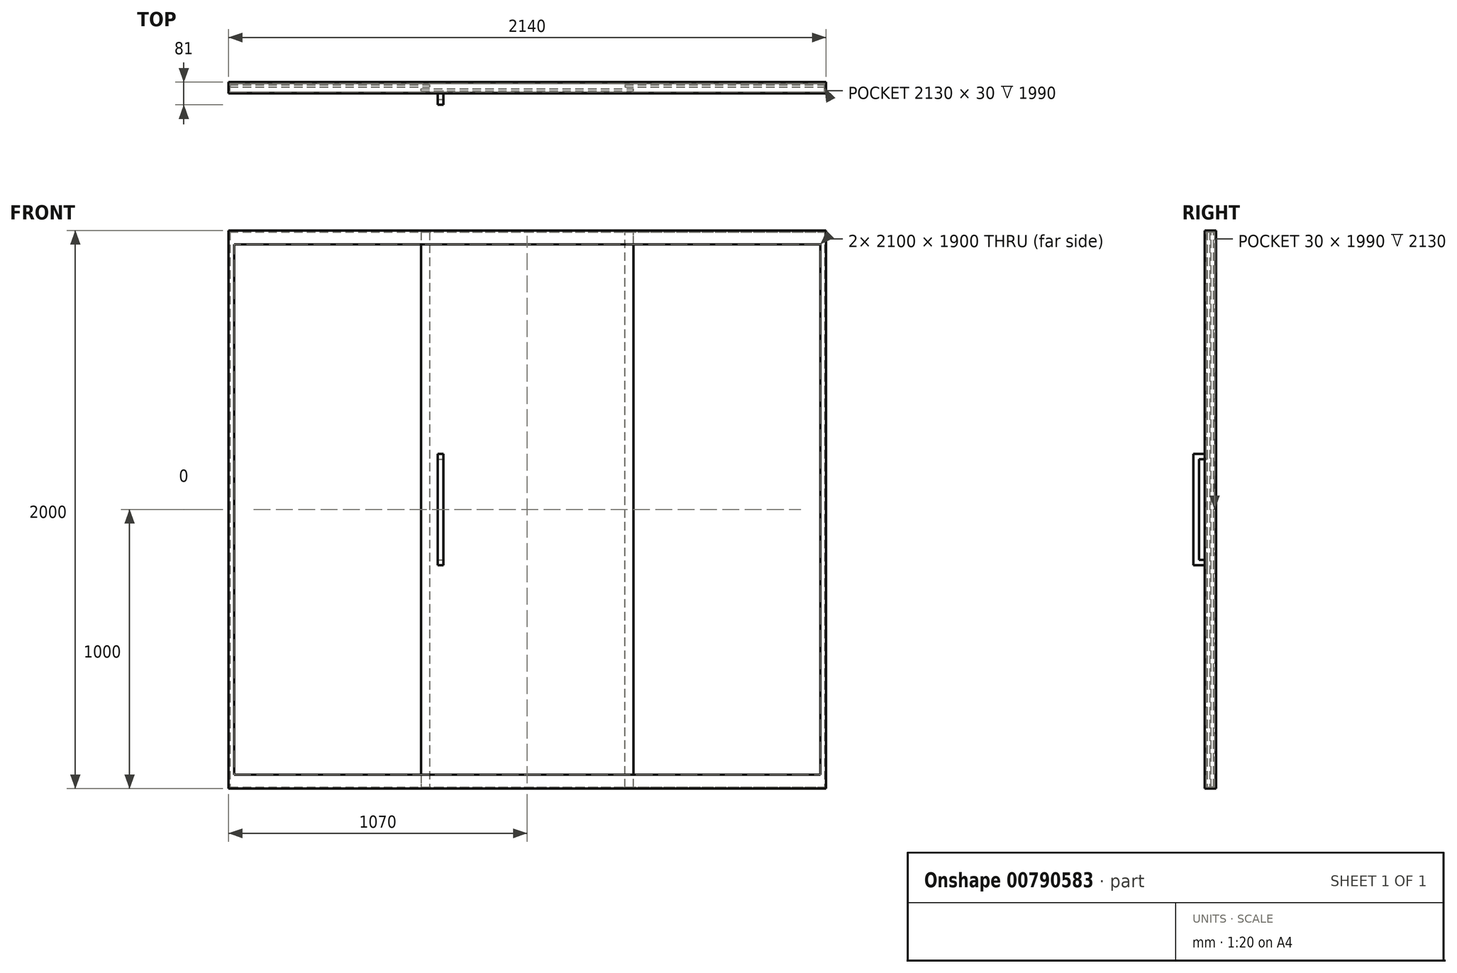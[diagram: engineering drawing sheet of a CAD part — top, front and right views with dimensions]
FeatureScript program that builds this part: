
annotation { "Feature Type Name" : "Feature", "Feature Type Description" : "" }
export const myFeature = defineFeature(function(context is Context, id is Id, definition is map)
    precondition{}
    {
        {
            var Q0;
            Q0=qCreatedBy(makeId("Front.planeOp"),FACE);
            var sketch = newSketch(context, id + "F0", { "sketchPlane" : qUnion([Q0])});
            skLineSegment(sketch, "E0.bottom", {"start": v(0, 0) * mm, "end": v(2140, 0) * mm});
            skLineSegment(sketch, "E0.top", {"start": v(0, 2000) * mm, "end": v(2140, 2000) * mm});
            skLineSegment(sketch, "E0.left", {"start": v(0, 0) * mm, "end": v(0, 2000) * mm});
            skLineSegment(sketch, "E0.right", {"start": v(2140, 0) * mm, "end": v(2140, 2000) * mm});
            skLineSegment(sketch, "E1.bottom", {"start": v(5, 1995) * mm, "end": v(2135, 1995) * mm});
            skLineSegment(sketch, "E1.top", {"start": v(5, 5) * mm, "end": v(2135, 5) * mm});
            skLineSegment(sketch, "E1.left", {"start": v(5, 1995) * mm, "end": v(5, 5) * mm});
            skLineSegment(sketch, "E1.right", {"start": v(2135, 1995) * mm, "end": v(2135, 5) * mm});
            skLineSegment(sketch, "E2.bottom", {"start": v(20, 1950) * mm, "end": v(2120, 1950) * mm});
            skLineSegment(sketch, "E2.top", {"start": v(20, 50) * mm, "end": v(2120, 50) * mm});
            skLineSegment(sketch, "E2.left", {"start": v(20, 1950) * mm, "end": v(20, 50) * mm});
            skLineSegment(sketch, "E2.right", {"start": v(2120, 1950) * mm, "end": v(2120, 50) * mm});
            skLineSegment(sketch, "E3", {"start": v(720, 1995) * mm, "end": v(720, 5) * mm});
            skLineSegment(sketch, "E4", {"start": v(1420, 5) * mm, "end": v(1420, 1995) * mm});
            skLineSegment(sketch, "E5", {"start": v(720, 1000) * mm, "end": v(5, 1000) * mm, "construction": true});
            skLineSegment(sketch, "E6", {"start": v(1420, 1000) * mm, "end": v(2135, 1000) * mm, "construction": true});
            skLineSegment(sketch, "E7", {"start": v(690, 1995) * mm, "end": v(690, 5) * mm});
            skLineSegment(sketch, "E8", {"start": v(1450, 5) * mm, "end": v(1450, 1995) * mm});
            skSolve(sketch);
        }
        {
            var Q0;
            {var subQ4=sQuery(id+"F0.wireOp",EDGE,"E1.left");Q0=makeQuery(id+"F0.imprint","IMPRINT",FACE,{"disambiguationData":[TD([[makeQuery(id+"F0.imprint","IMPRINT",EDGE,{"derivedFrom":subQ4}),1.0]])]});}
            var Q1;
            Q1=makeQuery(id+"F0.imprint","IMPRINT",FACE,{"disambiguationData":[TD([[makeQuery(id+"F0.imprint","IMPRINT",EDGE,{"derivedFrom":sQuery(id+"F0.wireOp",EDGE,"E0.bottom")}),1.0]])]});
            var Q2;
            {var subQ0=sQuery(id+"F0.wireOp",EDGE,"E3");var subQ1=sQuery(id+"F0.wireOp",EDGE,"E1.bottom");var subQ2=makeQuery(id+"F0.imprint","INTERSECT",VERTEX,{"derivedFrom":[subQ1,subQ0]});Q2=makeQuery(id+"F0.imprint","IMPRINT",FACE,{"disambiguationData":[TD([[makeQuery(id+"F0.imprint","IMPRINT",EDGE,{"disambiguationData":[TD([[subQ2,1.0]])],"derivedFrom":subQ1}),-1.0]])]});}
            var Q3;
            {var subQ0=sQuery(id+"F0.wireOp",EDGE,"E3");var subQ1=sQuery(id+"F0.wireOp",EDGE,"E1.bottom");var subQ2=makeQuery(id+"F0.imprint","INTERSECT",VERTEX,{"derivedFrom":[subQ1,subQ0]});Q3=makeQuery(id+"F0.imprint","IMPRINT",FACE,{"disambiguationData":[TD([[makeQuery(id+"F0.imprint","IMPRINT",EDGE,{"disambiguationData":[TD([[subQ2,-1.0]])],"derivedFrom":subQ1}),-1.0]])]});}
            var Q4;
            {var subQ4=sQuery(id+"F0.wireOp",EDGE,"E1.right");Q4=makeQuery(id+"F0.imprint","IMPRINT",FACE,{"disambiguationData":[TD([[makeQuery(id+"F0.imprint","IMPRINT",EDGE,{"derivedFrom":subQ4}),-1.0]])]});}
            var Q5;
            {var subQ0=sQuery(id+"F0.wireOp",EDGE,"E4");var subQ1=sQuery(id+"F0.wireOp",EDGE,"E1.bottom");var subQ2=makeQuery(id+"F0.imprint","INTERSECT",VERTEX,{"derivedFrom":[subQ1,subQ0]});Q5=makeQuery(id+"F0.imprint","IMPRINT",FACE,{"disambiguationData":[TD([[makeQuery(id+"F0.imprint","IMPRINT",EDGE,{"disambiguationData":[TD([[subQ2,-1.0]])],"derivedFrom":subQ1}),-1.0]])]});}
            var Q6;
            {var subQ0=sQuery(id+"F0.wireOp",EDGE,"E3");var subQ1=sQuery(id+"F0.wireOp",EDGE,"E1.top");var subQ2=makeQuery(id+"F0.imprint","INTERSECT",VERTEX,{"derivedFrom":[subQ1,subQ0]});Q6=makeQuery(id+"F0.imprint","IMPRINT",FACE,{"disambiguationData":[TD([[makeQuery(id+"F0.imprint","IMPRINT",EDGE,{"disambiguationData":[TD([[subQ2,1.0]])],"derivedFrom":subQ1}),1.0]])]});}
            var Q7;
            {var subQ0=sQuery(id+"F0.wireOp",EDGE,"E3");var subQ1=sQuery(id+"F0.wireOp",EDGE,"E1.top");var subQ2=makeQuery(id+"F0.imprint","INTERSECT",VERTEX,{"derivedFrom":[subQ1,subQ0]});Q7=makeQuery(id+"F0.imprint","IMPRINT",FACE,{"disambiguationData":[TD([[makeQuery(id+"F0.imprint","IMPRINT",EDGE,{"disambiguationData":[TD([[subQ2,-1.0]])],"derivedFrom":subQ1}),1.0]])]});}
            var Q8;
            {var subQ0=sQuery(id+"F0.wireOp",EDGE,"E4");var subQ1=sQuery(id+"F0.wireOp",EDGE,"E1.top");var subQ2=makeQuery(id+"F0.imprint","INTERSECT",VERTEX,{"derivedFrom":[subQ1,subQ0]});Q8=makeQuery(id+"F0.imprint","IMPRINT",FACE,{"disambiguationData":[TD([[makeQuery(id+"F0.imprint","IMPRINT",EDGE,{"disambiguationData":[TD([[subQ2,-1.0]])],"derivedFrom":subQ1}),1.0]])]});}
            extrude(context, id + "F1", {"entities" : qUnion([Q0, Q1, Q2, Q3, Q4, Q5, Q6, Q7, Q8]), "depth" : 20 * mm, "offsetDistance" : 25 * mm, "hasSecondDirection" : true, "secondDirectionOppositeDirection" : true, "secondDirectionDepth" : 20 * mm});
        }
        {
            var Q0;
            {var subQ4=sQuery(id+"F0.wireOp",EDGE,"E1.left");Q0=makeQuery(id+"F0.imprint","IMPRINT",FACE,{"disambiguationData":[TD([[makeQuery(id+"F0.imprint","IMPRINT",EDGE,{"derivedFrom":subQ4}),1.0]])]});}
            var Q1;
            {var subQ0=sQuery(id+"F0.wireOp",EDGE,"E3");var subQ1=sQuery(id+"F0.wireOp",EDGE,"E1.bottom");var subQ2=makeQuery(id+"F0.imprint","INTERSECT",VERTEX,{"derivedFrom":[subQ1,subQ0]});Q1=makeQuery(id+"F0.imprint","IMPRINT",FACE,{"disambiguationData":[TD([[makeQuery(id+"F0.imprint","IMPRINT",EDGE,{"disambiguationData":[TD([[subQ2,1.0]])],"derivedFrom":subQ1}),-1.0]])]});}
            var Q2;
            {var subQ0=sQuery(id+"F0.wireOp",EDGE,"E3");var subQ1=sQuery(id+"F0.wireOp",EDGE,"E1.bottom");var subQ2=makeQuery(id+"F0.imprint","INTERSECT",VERTEX,{"derivedFrom":[subQ1,subQ0]});Q2=makeQuery(id+"F0.imprint","IMPRINT",FACE,{"disambiguationData":[TD([[makeQuery(id+"F0.imprint","IMPRINT",EDGE,{"disambiguationData":[TD([[subQ2,-1.0]])],"derivedFrom":subQ1}),-1.0]])]});}
            var Q3;
            {var subQ0=sQuery(id+"F0.wireOp",EDGE,"E4");var subQ1=sQuery(id+"F0.wireOp",EDGE,"E1.bottom");var subQ2=makeQuery(id+"F0.imprint","INTERSECT",VERTEX,{"derivedFrom":[subQ1,subQ0]});Q3=makeQuery(id+"F0.imprint","IMPRINT",FACE,{"disambiguationData":[TD([[makeQuery(id+"F0.imprint","IMPRINT",EDGE,{"disambiguationData":[TD([[subQ2,-1.0]])],"derivedFrom":subQ1}),-1.0]])]});}
            var Q4;
            {var subQ4=sQuery(id+"F0.wireOp",EDGE,"E1.right");Q4=makeQuery(id+"F0.imprint","IMPRINT",FACE,{"disambiguationData":[TD([[makeQuery(id+"F0.imprint","IMPRINT",EDGE,{"derivedFrom":subQ4}),-1.0]])]});}
            var Q5;
            {var subQ0=sQuery(id+"F0.wireOp",EDGE,"E3");var subQ1=sQuery(id+"F0.wireOp",EDGE,"E1.top");var subQ2=makeQuery(id+"F0.imprint","INTERSECT",VERTEX,{"derivedFrom":[subQ1,subQ0]});Q5=makeQuery(id+"F0.imprint","IMPRINT",FACE,{"disambiguationData":[TD([[makeQuery(id+"F0.imprint","IMPRINT",EDGE,{"disambiguationData":[TD([[subQ2,1.0]])],"derivedFrom":subQ1}),1.0]])]});}
            var Q6;
            {var subQ0=sQuery(id+"F0.wireOp",EDGE,"E3");var subQ1=sQuery(id+"F0.wireOp",EDGE,"E1.top");var subQ2=makeQuery(id+"F0.imprint","INTERSECT",VERTEX,{"derivedFrom":[subQ1,subQ0]});Q6=makeQuery(id+"F0.imprint","IMPRINT",FACE,{"disambiguationData":[TD([[makeQuery(id+"F0.imprint","IMPRINT",EDGE,{"disambiguationData":[TD([[subQ2,-1.0]])],"derivedFrom":subQ1}),1.0]])]});}
            var Q7;
            {var subQ0=sQuery(id+"F0.wireOp",EDGE,"E4");var subQ1=sQuery(id+"F0.wireOp",EDGE,"E1.top");var subQ2=makeQuery(id+"F0.imprint","INTERSECT",VERTEX,{"derivedFrom":[subQ1,subQ0]});Q7=makeQuery(id+"F0.imprint","IMPRINT",FACE,{"disambiguationData":[TD([[makeQuery(id+"F0.imprint","IMPRINT",EDGE,{"disambiguationData":[TD([[subQ2,-1.0]])],"derivedFrom":subQ1}),1.0]])]});}
            extrude(context, id + "F2", {"entities" : qUnion([Q0, Q1, Q2, Q3, Q4, Q5, Q6, Q7]), "operationType" : NewBodyOperationType.REMOVE, "depth" : 15 * mm, "offsetDistance" : 25 * mm, "hasSecondDirection" : true, "secondDirectionOppositeDirection" : true, "secondDirectionDepth" : 15 * mm});
        }
        {
            var Q0;
            {var subQ0=sQuery(id+"F0.wireOp",EDGE,"E2.left");Q0=makeQuery(id+"F0.imprint","IMPRINT",FACE,{"disambiguationData":[TD([[makeQuery(id+"F0.imprint","IMPRINT",EDGE,{"derivedFrom":subQ0}),1.0]])]});}
            var Q1;
            {var subQ0=sQuery(id+"F0.wireOp",EDGE,"E2.right");Q1=makeQuery(id+"F0.imprint","IMPRINT",FACE,{"disambiguationData":[TD([[makeQuery(id+"F0.imprint","IMPRINT",EDGE,{"derivedFrom":subQ0}),-1.0]])]});}
            var Q2;
            {var subQ4=sQuery(id+"F0.wireOp",EDGE,"E1.right");Q2=makeQuery(id+"F0.imprint","IMPRINT",FACE,{"disambiguationData":[TD([[makeQuery(id+"F0.imprint","IMPRINT",EDGE,{"derivedFrom":subQ4}),-1.0]])]});}
            var Q3;
            {var subQ4=sQuery(id+"F0.wireOp",EDGE,"E1.left");Q3=makeQuery(id+"F0.imprint","IMPRINT",FACE,{"disambiguationData":[TD([[makeQuery(id+"F0.imprint","IMPRINT",EDGE,{"derivedFrom":subQ4}),1.0]])]});}
            var Q4;
            {var subQ0=sQuery(id+"F0.wireOp",EDGE,"E3");var subQ1=sQuery(id+"F0.wireOp",EDGE,"E1.bottom");var subQ2=makeQuery(id+"F0.imprint","INTERSECT",VERTEX,{"derivedFrom":[subQ1,subQ0]});Q4=makeQuery(id+"F0.imprint","IMPRINT",FACE,{"disambiguationData":[TD([[makeQuery(id+"F0.imprint","IMPRINT",EDGE,{"disambiguationData":[TD([[subQ2,1.0]])],"derivedFrom":subQ1}),-1.0]])]});}
            var Q5;
            {var subQ0=sQuery(id+"F0.wireOp",EDGE,"E7");var subQ1=sQuery(id+"F0.wireOp",EDGE,"E2.bottom");var subQ2=makeQuery(id+"F0.imprint","INTERSECT",VERTEX,{"derivedFrom":[subQ1,subQ0]});Q5=makeQuery(id+"F0.imprint","IMPRINT",FACE,{"disambiguationData":[TD([[makeQuery(id+"F0.imprint","IMPRINT",EDGE,{"disambiguationData":[TD([[subQ2,-1.0]])],"derivedFrom":subQ1}),-1.0]])]});}
            var Q6;
            {var subQ0=sQuery(id+"F0.wireOp",EDGE,"E4");var subQ1=sQuery(id+"F0.wireOp",EDGE,"E1.bottom");var subQ2=makeQuery(id+"F0.imprint","INTERSECT",VERTEX,{"derivedFrom":[subQ1,subQ0]});Q6=makeQuery(id+"F0.imprint","IMPRINT",FACE,{"disambiguationData":[TD([[makeQuery(id+"F0.imprint","IMPRINT",EDGE,{"disambiguationData":[TD([[subQ2,-1.0]])],"derivedFrom":subQ1}),-1.0]])]});}
            var Q7;
            {var subQ0=sQuery(id+"F0.wireOp",EDGE,"E4");var subQ1=sQuery(id+"F0.wireOp",EDGE,"E2.bottom");var subQ2=makeQuery(id+"F0.imprint","INTERSECT",VERTEX,{"derivedFrom":[subQ1,subQ0]});Q7=makeQuery(id+"F0.imprint","IMPRINT",FACE,{"disambiguationData":[TD([[makeQuery(id+"F0.imprint","IMPRINT",EDGE,{"disambiguationData":[TD([[subQ2,-1.0]])],"derivedFrom":subQ1}),-1.0]])]});}
            var Q8;
            {var subQ0=sQuery(id+"F0.wireOp",EDGE,"E4");var subQ1=sQuery(id+"F0.wireOp",EDGE,"E1.top");var subQ2=makeQuery(id+"F0.imprint","INTERSECT",VERTEX,{"derivedFrom":[subQ1,subQ0]});Q8=makeQuery(id+"F0.imprint","IMPRINT",FACE,{"disambiguationData":[TD([[makeQuery(id+"F0.imprint","IMPRINT",EDGE,{"disambiguationData":[TD([[subQ2,-1.0]])],"derivedFrom":subQ1}),1.0]])]});}
            var Q9;
            {var subQ0=sQuery(id+"F0.wireOp",EDGE,"E3");var subQ1=sQuery(id+"F0.wireOp",EDGE,"E1.top");var subQ2=makeQuery(id+"F0.imprint","INTERSECT",VERTEX,{"derivedFrom":[subQ1,subQ0]});Q9=makeQuery(id+"F0.imprint","IMPRINT",FACE,{"disambiguationData":[TD([[makeQuery(id+"F0.imprint","IMPRINT",EDGE,{"disambiguationData":[TD([[subQ2,1.0]])],"derivedFrom":subQ1}),1.0]])]});}
            extrude(context, id + "F3", {"entities" : qUnion([Q0, Q1, Q2, Q3, Q4, Q5, Q6, Q7, Q8, Q9]), "oppositeDirection" : true, "depth" : 11 * mm, "offsetDistance" : 25 * mm, "hasSecondDirection" : true, "secondDirectionOppositeDirection" : true, "secondDirectionDepth" : 3 * mm});
        }
        {
            var Q0;
            {var subQ0=sQuery(id+"F0.wireOp",EDGE,"E3");var subQ1=sQuery(id+"F0.wireOp",EDGE,"E1.bottom");var subQ2=makeQuery(id+"F0.imprint","INTERSECT",VERTEX,{"derivedFrom":[subQ1,subQ0]});Q0=makeQuery(id+"F0.imprint","IMPRINT",FACE,{"disambiguationData":[TD([[makeQuery(id+"F0.imprint","IMPRINT",EDGE,{"disambiguationData":[TD([[subQ2,-1.0]])],"derivedFrom":subQ1}),-1.0]])]});}
            var Q1;
            {var subQ0=sQuery(id+"F0.wireOp",EDGE,"E3");var subQ1=sQuery(id+"F0.wireOp",EDGE,"E2.bottom");var subQ2=makeQuery(id+"F0.imprint","INTERSECT",VERTEX,{"derivedFrom":[subQ1,subQ0]});Q1=makeQuery(id+"F0.imprint","IMPRINT",FACE,{"disambiguationData":[TD([[makeQuery(id+"F0.imprint","IMPRINT",EDGE,{"disambiguationData":[TD([[subQ2,-1.0]])],"derivedFrom":subQ1}),-1.0]])]});}
            var Q2;
            {var subQ0=sQuery(id+"F0.wireOp",EDGE,"E4");var subQ1=sQuery(id+"F0.wireOp",EDGE,"E1.bottom");var subQ2=makeQuery(id+"F0.imprint","INTERSECT",VERTEX,{"derivedFrom":[subQ1,subQ0]});Q2=makeQuery(id+"F0.imprint","IMPRINT",FACE,{"disambiguationData":[TD([[makeQuery(id+"F0.imprint","IMPRINT",EDGE,{"disambiguationData":[TD([[subQ2,-1.0]])],"derivedFrom":subQ1}),-1.0]])]});}
            var Q3;
            {var subQ0=sQuery(id+"F0.wireOp",EDGE,"E4");var subQ1=sQuery(id+"F0.wireOp",EDGE,"E2.bottom");var subQ2=makeQuery(id+"F0.imprint","INTERSECT",VERTEX,{"derivedFrom":[subQ1,subQ0]});Q3=makeQuery(id+"F0.imprint","IMPRINT",FACE,{"disambiguationData":[TD([[makeQuery(id+"F0.imprint","IMPRINT",EDGE,{"disambiguationData":[TD([[subQ2,-1.0]])],"derivedFrom":subQ1}),-1.0]])]});}
            var Q4;
            {var subQ0=sQuery(id+"F0.wireOp",EDGE,"E3");var subQ1=sQuery(id+"F0.wireOp",EDGE,"E1.bottom");var subQ2=makeQuery(id+"F0.imprint","INTERSECT",VERTEX,{"derivedFrom":[subQ1,subQ0]});Q4=makeQuery(id+"F0.imprint","IMPRINT",FACE,{"disambiguationData":[TD([[makeQuery(id+"F0.imprint","IMPRINT",EDGE,{"disambiguationData":[TD([[subQ2,1.0]])],"derivedFrom":subQ1}),-1.0]])]});}
            var Q5;
            {var subQ0=sQuery(id+"F0.wireOp",EDGE,"E7");var subQ1=sQuery(id+"F0.wireOp",EDGE,"E2.bottom");var subQ2=makeQuery(id+"F0.imprint","INTERSECT",VERTEX,{"derivedFrom":[subQ1,subQ0]});Q5=makeQuery(id+"F0.imprint","IMPRINT",FACE,{"disambiguationData":[TD([[makeQuery(id+"F0.imprint","IMPRINT",EDGE,{"disambiguationData":[TD([[subQ2,-1.0]])],"derivedFrom":subQ1}),-1.0]])]});}
            var Q6;
            {var subQ0=sQuery(id+"F0.wireOp",EDGE,"E3");var subQ1=sQuery(id+"F0.wireOp",EDGE,"E1.top");var subQ2=makeQuery(id+"F0.imprint","INTERSECT",VERTEX,{"derivedFrom":[subQ1,subQ0]});Q6=makeQuery(id+"F0.imprint","IMPRINT",FACE,{"disambiguationData":[TD([[makeQuery(id+"F0.imprint","IMPRINT",EDGE,{"disambiguationData":[TD([[subQ2,1.0]])],"derivedFrom":subQ1}),1.0]])]});}
            var Q7;
            {var subQ0=sQuery(id+"F0.wireOp",EDGE,"E3");var subQ1=sQuery(id+"F0.wireOp",EDGE,"E1.top");var subQ2=makeQuery(id+"F0.imprint","INTERSECT",VERTEX,{"derivedFrom":[subQ1,subQ0]});Q7=makeQuery(id+"F0.imprint","IMPRINT",FACE,{"disambiguationData":[TD([[makeQuery(id+"F0.imprint","IMPRINT",EDGE,{"disambiguationData":[TD([[subQ2,-1.0]])],"derivedFrom":subQ1}),1.0]])]});}
            var Q8;
            {var subQ0=sQuery(id+"F0.wireOp",EDGE,"E4");var subQ1=sQuery(id+"F0.wireOp",EDGE,"E1.top");var subQ2=makeQuery(id+"F0.imprint","INTERSECT",VERTEX,{"derivedFrom":[subQ1,subQ0]});Q8=makeQuery(id+"F0.imprint","IMPRINT",FACE,{"disambiguationData":[TD([[makeQuery(id+"F0.imprint","IMPRINT",EDGE,{"disambiguationData":[TD([[subQ2,-1.0]])],"derivedFrom":subQ1}),1.0]])]});}
            extrude(context, id + "F4", {"entities" : qUnion([Q0, Q1, Q2, Q3, Q4, Q5, Q6, Q7, Q8]), "depth" : 11 * mm, "offsetDistance" : 25 * mm, "hasSecondDirection" : true, "secondDirectionOppositeDirection" : false, "secondDirectionDepth" : 3 * mm});
        }
        {
            var Q0;
            Q0=makeQuery(id+"F4.opExtrude","CAP_FACE",FACE,{"disambiguationData":[OSD([sQuery(id+"F0.wireOp",EDGE,"E1.bottom"),sQuery(id+"F0.wireOp",EDGE,"E1.top"),sQuery(id+"F0.wireOp",EDGE,"E7"),sQuery(id+"F0.wireOp",EDGE,"E8")])],"isStart":false});
            var sketch = newSketch(context, id + "F5", { "sketchPlane" : qUnion([Q0])});
            skLineSegment(sketch, "E9.bottom", {"start": v(750, 1200) * mm, "end": v(770, 1200) * mm});
            skLineSegment(sketch, "E9.top", {"start": v(750, 1180) * mm, "end": v(770, 1180) * mm});
            skLineSegment(sketch, "E9.left", {"start": v(750, 1200) * mm, "end": v(750, 1180) * mm});
            skLineSegment(sketch, "E9.right", {"start": v(770, 1200) * mm, "end": v(770, 1180) * mm});
            skLineSegment(sketch, "E10.bottom", {"start": v(750, 820) * mm, "end": v(770, 820) * mm});
            skLineSegment(sketch, "E10.top", {"start": v(750, 800) * mm, "end": v(770, 800) * mm});
            skLineSegment(sketch, "E10.left", {"start": v(750, 820) * mm, "end": v(750, 800) * mm});
            skLineSegment(sketch, "E10.right", {"start": v(770, 820) * mm, "end": v(770, 800) * mm});
            skLineSegment(sketch, "E11", {"start": v(750, 1180) * mm, "end": v(750, 820) * mm});
            skLineSegment(sketch, "E12", {"start": v(770, 1180) * mm, "end": v(770, 820) * mm});
            skLineSegment(sketch, "E13", {"start": v(750, 1000) * mm, "end": v(750, 0) * mm, "construction": true});
            skLineSegment(sketch, "E14", {"start": v(750, 0) * mm, "end": v(0, 0) * mm, "construction": true});
            skSolve(sketch);
        }
        {
            var Q0;
            Q0=makeQuery(id+"F5.imprint","IMPRINT",FACE,{"disambiguationData":[TD([[makeQuery(id+"F5.imprint","IMPRINT",EDGE,{"derivedFrom":sQuery(id+"F5.wireOp",EDGE,"E9.bottom")}),-1.0]])]});
            var Q1;
            Q1=makeQuery(id+"F5.imprint","IMPRINT",FACE,{"disambiguationData":[TD([[makeQuery(id+"F5.imprint","IMPRINT",EDGE,{"derivedFrom":sQuery(id+"F5.wireOp",EDGE,"E10.bottom")}),-1.0]])]});
            extrude(context, id + "F6", {"entities" : qUnion([Q0, Q1]), "depth" : 50 * mm, "offsetDistance" : 25 * mm});
        }
        {
            var Q0;
            Q0=makeQuery(id+"F5.imprint","IMPRINT",FACE,{"disambiguationData":[TD([[makeQuery(id+"F5.imprint","IMPRINT",EDGE,{"derivedFrom":sQuery(id+"F5.wireOp",EDGE,"E9.top")}),-1.0]])]});
            extrude(context, id + "F7", {"entities" : qUnion([Q0]), "operationType" : NewBodyOperationType.ADD, "depth" : 50 * mm, "offsetDistance" : 25 * mm, "hasSecondDirection" : true, "secondDirectionOppositeDirection" : false, "secondDirectionDepth" : 30 * mm});
        }
    });
